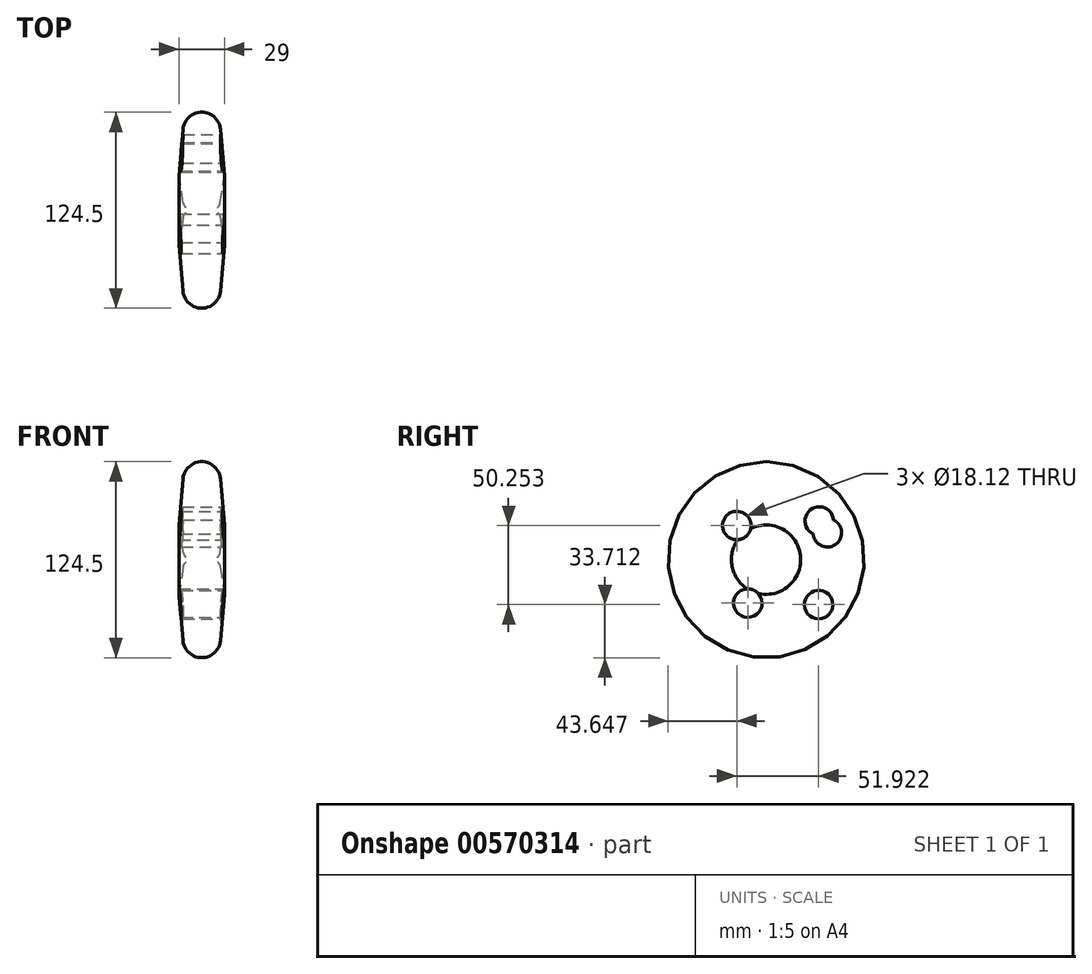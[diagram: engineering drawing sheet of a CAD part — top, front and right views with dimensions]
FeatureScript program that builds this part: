
annotation { "Feature Type Name" : "Feature", "Feature Type Description" : "" }
export const myFeature = defineFeature(function(context is Context, id is Id, definition is map)
    precondition{}
    {
        {
            var Q0;
            Q0=qCreatedBy(makeId("Top.planeOp"),FACE);
            var sketch = newSketch(context, id + "F0", { "sketchPlane" : qUnion([Q0])});
            skArc(sketch, "E0", {"start": v(-11.95, -1.04) * mm, "mid": v(0, -12) * mm, "end": v(11.95, -1.04) * mm});
            skLineSegment(sketch, "E1", {"start": v(0, 50.25) * mm, "end": v(6.43, 50.25) * mm});
            skLineSegment(sketch, "E2", {"start": v(0, 50.25) * mm, "end": v(-6.43, 50.25) * mm});
            skLineSegment(sketch, "E3", {"start": v(9.96, 48.79) * mm, "end": v(10.35, 48.4) * mm});
            skLineSegment(sketch, "E4", {"start": v(11.75, 45.64) * mm, "end": v(14.5, 28.25) * mm});
            skLineSegment(sketch, "E5", {"start": v(-9.96, 48.79) * mm, "end": v(-10.35, 48.4) * mm});
            skLineSegment(sketch, "E6", {"start": v(-11.75, 45.64) * mm, "end": v(-14.5, 28.25) * mm});
            skLineSegment(sketch, "E7", {"start": v(14.5, 28.25) * mm, "end": v(11.95, -1.04) * mm});
            skLineSegment(sketch, "E8", {"start": v(-14.5, 28.25) * mm, "end": v(-11.95, -1.04) * mm});
            skPoint(sketch, "E9.start.orphan", {"position": v(0, -12) * mm});
            skPoint(sketch, "E10.visualSharp", {"position": v(8.5, 50.25) * mm});
            skArc(sketch, "E10.filletArc", {"start": v(9.96, 48.79) * mm, "mid": v(8.34, 49.87) * mm, "end": v(6.43, 50.25) * mm});
            skPoint(sketch, "E11.visualSharp", {"position": v(-8.5, 50.25) * mm});
            skArc(sketch, "E11.filletArc", {"start": v(-6.43, 50.25) * mm, "mid": v(-8.34, 49.87) * mm, "end": v(-9.96, 48.79) * mm});
            skPoint(sketch, "E12.visualSharp", {"position": v(11.5, 47.25) * mm});
            skArc(sketch, "E12.filletArc", {"start": v(11.75, 45.64) * mm, "mid": v(11.27, 47.13) * mm, "end": v(10.35, 48.4) * mm});
            skPoint(sketch, "E13.visualSharp", {"position": v(-11.5, 47.25) * mm});
            skArc(sketch, "E13.filletArc", {"start": v(-10.35, 48.4) * mm, "mid": v(-11.27, 47.13) * mm, "end": v(-11.75, 45.64) * mm});
            skSolve(sketch);
        }
        {
            var Q0;
            Q0=makeQuery(id+"F0.imprint","IMPRINT",FACE,{"disambiguationData":[TD([[makeQuery(id+"F0.imprint","IMPRINT",EDGE,{"derivedFrom":sQuery(id+"F0.wireOp",EDGE,"E0")}),1.0]])]});
            var Q1;
            Q1=sQuery(id+"F0.wireOp",EDGE,"E1");
            revolve(context, id + "F1", {"entities" : qUnion([Q0]), "axis" : qUnion([Q1]), "revolveType" : RevolveType.FULL});
        }
        {
            var Q0;
            Q0=qCreatedBy(makeId("Right.planeOp"),FACE);
            var sketch = newSketch(context, id + "F2", { "sketchPlane" : qUnion([Q0])});
            skCircle(sketch, "E14", {"center": v(89.16, 17.1) * mm, "radius": 9.06 * mm});
            skCircle(sketch, "E15", {"center": v(38.63, -27.59) * mm, "radius": 9.06 * mm});
            skCircle(sketch, "E16", {"center": v(83.57, -28.54) * mm, "radius": 9.06 * mm});
            skCircle(sketch, "E17", {"center": v(31.65, 21.71) * mm, "radius": 9.06 * mm});
            skCircle(sketch, "E18", {"center": v(84.01, 24.56) * mm, "radius": 9.06 * mm});
            skSolve(sketch);
        }
        {
            var Q0;
            Q0 = qSketchRegion(id + "F2", true);
            extrude(context, id + "F3", {"entities" : qUnion([Q0]), "operationType" : NewBodyOperationType.REMOVE, "endBound" : BoundingType.SYMMETRIC, "oppositeDirection" : true, "depth" : 50 * mm, "offsetDistance" : 25 * mm});
        }
    });
